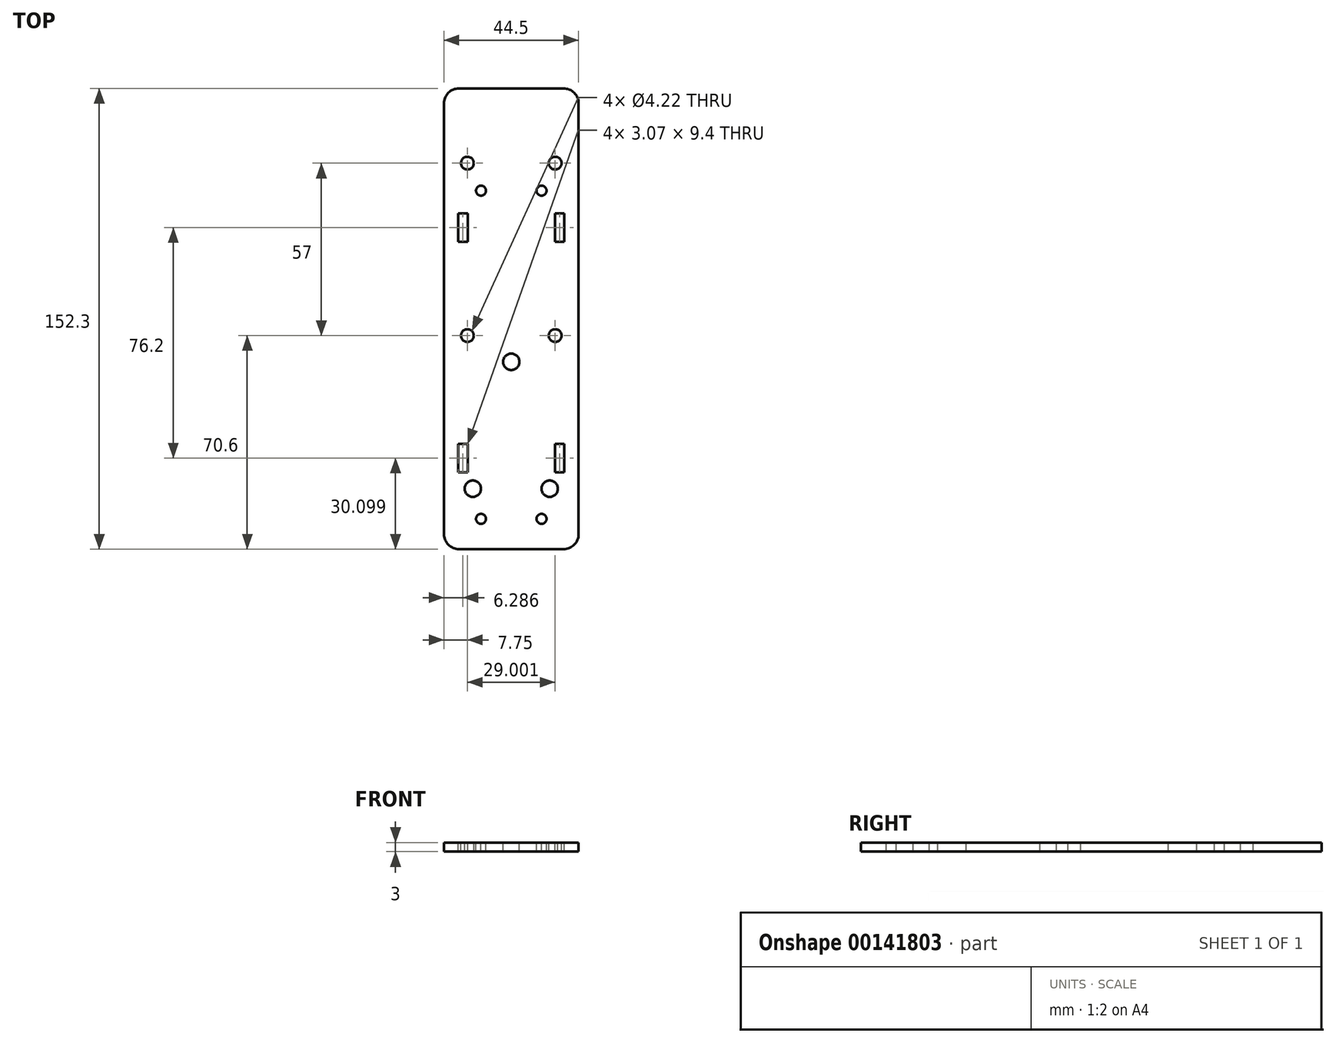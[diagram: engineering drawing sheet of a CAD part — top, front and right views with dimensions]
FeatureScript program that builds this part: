
annotation { "Feature Type Name" : "Feature", "Feature Type Description" : "" }
export const myFeature = defineFeature(function(context is Context, id is Id, definition is map)
    precondition{}
    {
        {
            var Q0;
            Q0=qCreatedBy(makeId("Top.planeOp"),FACE);
            var sketch = newSketch(context, id + "F0", { "sketchPlane" : qUnion([Q0])});
            skLineSegment(sketch, "E0.bottom", {"start": v(17.25, -78) * mm, "end": v(-17.25, -78) * mm});
            skLineSegment(sketch, "E0.top", {"start": v(17.25, 78) * mm, "end": v(-17.25, 78) * mm});
            skLineSegment(sketch, "E0.left", {"start": v(22.25, -73) * mm, "end": v(22.25, 73) * mm});
            skLineSegment(sketch, "E0.right", {"start": v(-22.25, -73) * mm, "end": v(-22.25, 73) * mm});
            skPoint(sketch, "E0.middle", {"position": v(0, 0) * mm});
            skPoint(sketch, "E1.visualSharp", {"position": v(-22.25, -78) * mm});
            skArc(sketch, "E1.filletArc", {"start": v(-22.25, -73) * mm, "mid": v(-20.79, -76.54) * mm, "end": v(-17.25, -78) * mm});
            skPoint(sketch, "E2.visualSharp", {"position": v(22.25, -78) * mm});
            skArc(sketch, "E2.filletArc", {"start": v(17.25, -78) * mm, "mid": v(20.79, -76.54) * mm, "end": v(22.25, -73) * mm});
            skPoint(sketch, "E3.visualSharp", {"position": v(-22.25, 78) * mm});
            skArc(sketch, "E3.filletArc", {"start": v(-17.25, 78) * mm, "mid": v(-20.79, 76.54) * mm, "end": v(-22.25, 73) * mm});
            skPoint(sketch, "E4.visualSharp", {"position": v(22.25, 78) * mm});
            skArc(sketch, "E4.filletArc", {"start": v(22.25, 73) * mm, "mid": v(20.79, 76.54) * mm, "end": v(17.25, 78) * mm});
            skSolve(sketch);
        }
        {
            var Q0;
            Q0 = qSketchRegion(id + "F0", true);
            extrude(context, id + "F1", {"entities" : qUnion([Q0]), "oppositeDirection" : true, "depth" : 3 * mm});
        }
        {
            var Q0;
            Q0=makeQuery(id+"F1.opExtrude","CAP_FACE",FACE,{"disambiguationData":[OSD([sQuery(id+"F0.wireOp",EDGE,"E0.bottom"),sQuery(id+"F0.wireOp",EDGE,"E0.top"),sQuery(id+"F0.wireOp",EDGE,"E0.left"),sQuery(id+"F0.wireOp",EDGE,"E0.right"),sQuery(id+"F0.wireOp",EDGE,"E1.filletArc"),sQuery(id+"F0.wireOp",EDGE,"E2.filletArc"),sQuery(id+"F0.wireOp",EDGE,"E3.filletArc"),sQuery(id+"F0.wireOp",EDGE,"E4.filletArc")])],"isStart":true});
            var sketch = newSketch(context, id + "F2", { "sketchPlane" : qUnion([Q0])});
            skLineSegment(sketch, "E5.0", {"start": v(17.25, 78) * mm, "end": v(-17.25, 78) * mm});
            skLineSegment(sketch, "E5.1", {"start": v(-22.25, -73) * mm, "end": v(-22.25, 73) * mm});
            skLineSegment(sketch, "E5.2", {"start": v(22.25, -73) * mm, "end": v(22.25, 73) * mm});
            skLineSegment(sketch, "E5.3", {"start": v(17.25, -78) * mm, "end": v(-17.25, -78) * mm});
            skCircle(sketch, "E6", {"center": v(-10, -68) * mm, "radius": 1.65 * mm});
            skCircle(sketch, "E7", {"center": v(-12.7, -58.02) * mm, "radius": 2.7 * mm});
            skCircle(sketch, "E8", {"center": v(-14.5, -7.4) * mm, "radius": 2.1 * mm});
            skCircle(sketch, "E9", {"center": v(-10, 40.5) * mm, "radius": 1.65 * mm});
            skCircle(sketch, "E10", {"center": v(-14.5, 49.6) * mm, "radius": 2.1 * mm});
            skLineSegment(sketch, "E11", {"start": v(0, -78) * mm, "end": v(0, 78) * mm});
            skCircle(sketch, "E12.MirrorC", {"center": v(10, -68) * mm, "radius": 1.65 * mm});
            skCircle(sketch, "E13.MirrorC", {"center": v(12.7, -58.02) * mm, "radius": 2.7 * mm});
            skCircle(sketch, "E14.MirrorC", {"center": v(14.5, -7.4) * mm, "radius": 2.1 * mm});
            skCircle(sketch, "E15.MirrorC", {"center": v(10, 40.5) * mm, "radius": 1.65 * mm});
            skCircle(sketch, "E16.MirrorC", {"center": v(14.5, 49.6) * mm, "radius": 2.1 * mm});
            skCircle(sketch, "E17", {"center": v(0, -16.08) * mm, "radius": 2.7 * mm});
            skLineSegment(sketch, "E18.bottom", {"start": v(-17.5, -52.6) * mm, "end": v(-14.43, -52.6) * mm});
            skLineSegment(sketch, "E18.top", {"start": v(-17.5, -43.2) * mm, "end": v(-14.43, -43.2) * mm});
            skLineSegment(sketch, "E18.left", {"start": v(-17.5, -52.6) * mm, "end": v(-17.5, -43.2) * mm});
            skLineSegment(sketch, "E18.right", {"start": v(-14.43, -52.6) * mm, "end": v(-14.43, -43.2) * mm});
            skLineSegment(sketch, "E19.bottom", {"start": v(-17.5, 23.6) * mm, "end": v(-14.43, 23.6) * mm});
            skLineSegment(sketch, "E19.left", {"start": v(-17.5, 23.6) * mm, "end": v(-17.5, 33) * mm});
            skLineSegment(sketch, "E19.right", {"start": v(-14.43, 23.6) * mm, "end": v(-14.43, 33) * mm});
            skLineSegment(sketch, "E20", {"start": v(-14.43, 33) * mm, "end": v(-17.5, 33) * mm});
            skLineSegment(sketch, "E21.MirrorCS", {"start": v(17.5, 23.6) * mm, "end": v(14.43, 23.6) * mm});
            skLineSegment(sketch, "E22.MirrorCS", {"start": v(14.43, 23.6) * mm, "end": v(14.43, 33) * mm});
            skLineSegment(sketch, "E23.MirrorCS", {"start": v(14.43, 33) * mm, "end": v(17.5, 33) * mm});
            skLineSegment(sketch, "E24.MirrorCS", {"start": v(17.5, 23.6) * mm, "end": v(17.5, 33) * mm});
            skLineSegment(sketch, "E25.MirrorCS", {"start": v(14.43, -52.6) * mm, "end": v(14.43, -43.2) * mm});
            skLineSegment(sketch, "E26.MirrorCS", {"start": v(17.5, -43.2) * mm, "end": v(14.43, -43.2) * mm});
            skLineSegment(sketch, "E27.MirrorCS", {"start": v(17.5, -52.6) * mm, "end": v(17.5, -43.2) * mm});
            skLineSegment(sketch, "E28.MirrorCS", {"start": v(17.5, -52.6) * mm, "end": v(14.43, -52.6) * mm});
            skSolve(sketch);
        }
        {
            var Q0;
            Q0 = qSketchRegion(id + "F2", true);
            extrude(context, id + "F3", {"entities" : qUnion([Q0]), "operationType" : NewBodyOperationType.REMOVE, "endBound" : BoundingType.THROUGH_ALL, "oppositeDirection" : true, "depth" : 25.4 * mm});
        }
        {
            var Q0;
            Q0=makeQuery(id+"F1.opExtrude","CAP_FACE",FACE,{"disambiguationData":[OSD([sQuery(id+"F0.wireOp",EDGE,"E0.bottom"),sQuery(id+"F0.wireOp",EDGE,"E0.top"),sQuery(id+"F0.wireOp",EDGE,"E0.left"),sQuery(id+"F0.wireOp",EDGE,"E0.right"),sQuery(id+"F0.wireOp",EDGE,"E1.filletArc"),sQuery(id+"F0.wireOp",EDGE,"E2.filletArc"),sQuery(id+"F0.wireOp",EDGE,"E3.filletArc"),sQuery(id+"F0.wireOp",EDGE,"E4.filletArc")])],"isStart":true});
            var sketch = newSketch(context, id + "F4", { "sketchPlane" : qUnion([Q0])});
            skLineSegment(sketch, "E29", {"start": v(-17.25, 74.3) * mm, "end": v(17.25, 74.3) * mm});
            skLineSegment(sketch, "E30.0", {"start": v(-22.25, -73) * mm, "end": v(-22.25, 69.3) * mm});
            skLineSegment(sketch, "E30.1", {"start": v(17.25, 78) * mm, "end": v(-17.25, 78) * mm});
            skLineSegment(sketch, "E30.2", {"start": v(22.25, -73) * mm, "end": v(22.25, 69.3) * mm});
            skPoint(sketch, "E31.newPointA", {"position": v(-22.25, 73) * mm});
            skArc(sketch, "E31.filletArc", {"start": v(-17.25, 74.3) * mm, "mid": v(-20.79, 72.83) * mm, "end": v(-22.25, 69.3) * mm});
            skPoint(sketch, "E32.newPointB", {"position": v(22.25, 73) * mm});
            skArc(sketch, "E32.filletArc", {"start": v(22.25, 69.3) * mm, "mid": v(20.79, 72.83) * mm, "end": v(17.25, 74.3) * mm});
            skSolve(sketch);
        }
        {
            var Q0;
            Q0 = qSketchRegion(id + "F4", true);
            var Q1;
            Q1=makeQuery(id+"F4.imprint","IMPRINT",FACE,{"disambiguationData":[TD([[makeQuery(id+"F4.imprint","IMPRINT",EDGE,{"derivedFrom":sQuery(id+"F4.wireOp",EDGE,"E29")}),1.0]])]});
            extrude(context, id + "F5", {"entities" : qUnion([Q0, Q1]), "operationType" : NewBodyOperationType.REMOVE, "endBound" : BoundingType.THROUGH_ALL, "oppositeDirection" : true, "depth" : 25.4 * mm});
        }
    });
